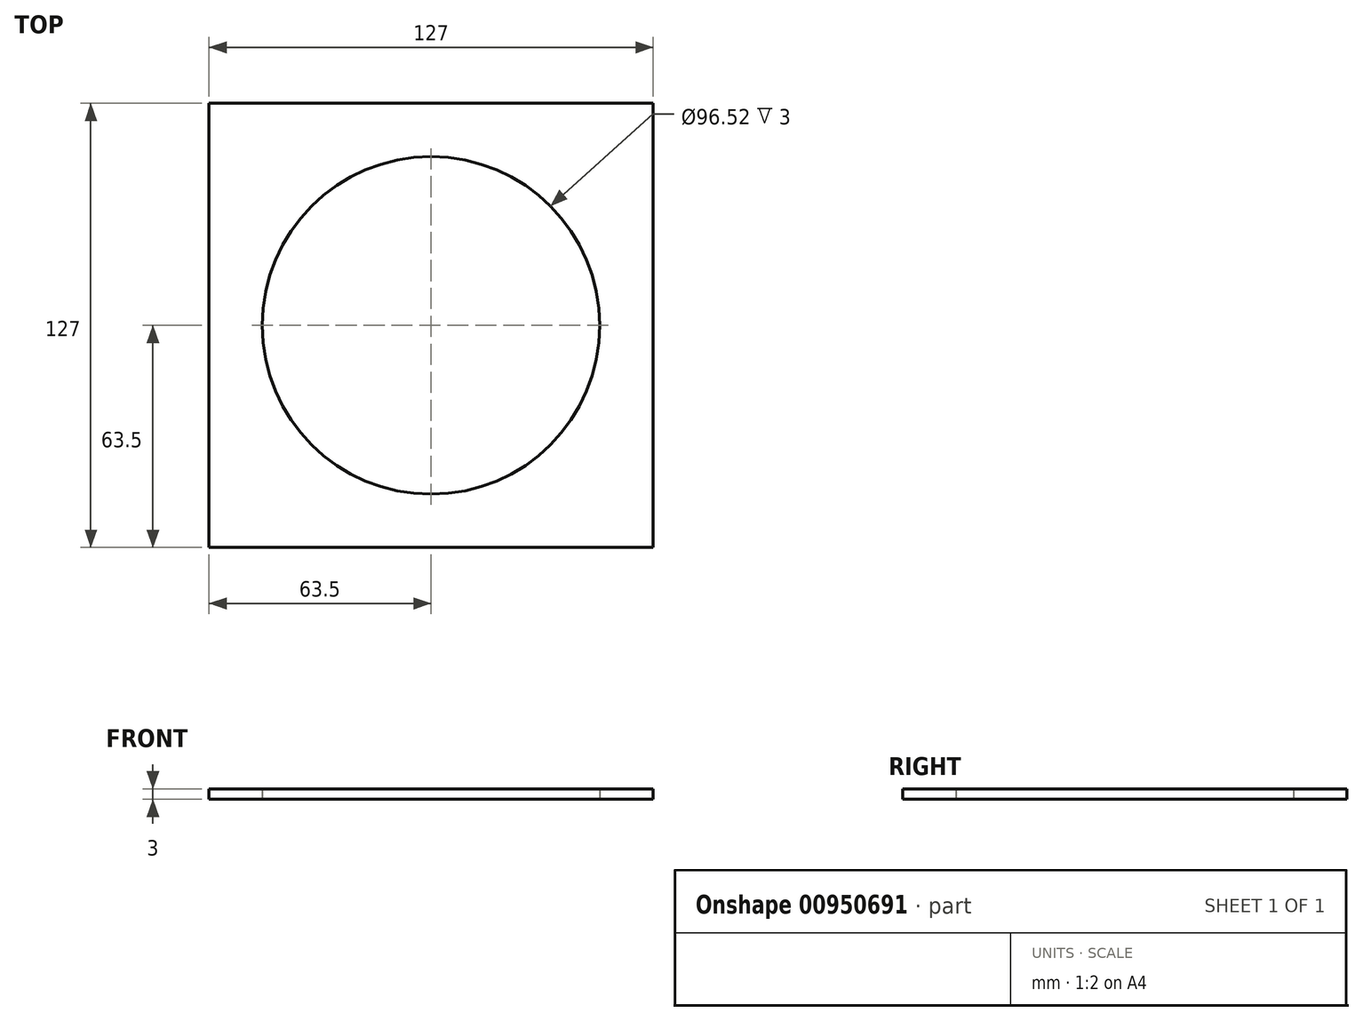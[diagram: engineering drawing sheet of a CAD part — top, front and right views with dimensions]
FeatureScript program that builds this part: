
annotation { "Feature Type Name" : "Feature", "Feature Type Description" : "" }
export const myFeature = defineFeature(function(context is Context, id is Id, definition is map)
    precondition{}
    {
        {
            var Q0;
            Q0=qCreatedBy(makeId("Top.planeOp"),FACE);
            var sketch = newSketch(context, id + "F0", { "sketchPlane" : qUnion([Q0])});
            skLineSegment(sketch, "E0.bottom", {"start": v(63.5, 63.5) * mm, "end": v(-63.5, 63.5) * mm});
            skLineSegment(sketch, "E0.top", {"start": v(63.5, -63.5) * mm, "end": v(-63.5, -63.5) * mm});
            skLineSegment(sketch, "E0.left", {"start": v(63.5, 63.5) * mm, "end": v(63.5, -63.5) * mm});
            skLineSegment(sketch, "E0.right", {"start": v(-63.5, 63.5) * mm, "end": v(-63.5, -63.5) * mm});
            skPoint(sketch, "E0.middle", {"position": v(0, 0) * mm});
            skCircle(sketch, "E1", {"center": v(0, 0) * mm, "radius": 48.26 * mm});
            skSolve(sketch);
        }
        {
            var Q0;
            Q0=makeQuery(id+"F0.imprint","IMPRINT",FACE,{"disambiguationData":[TD([[makeQuery(id+"F0.imprint","IMPRINT",EDGE,{"derivedFrom":sQuery(id+"F0.wireOp",EDGE,"E0.bottom")}),1.0]])]});
            extrude(context, id + "F1", {"entities" : qUnion([Q0]), "depth" : 3 * mm, "offsetDistance" : 25.4 * mm});
        }
    });
